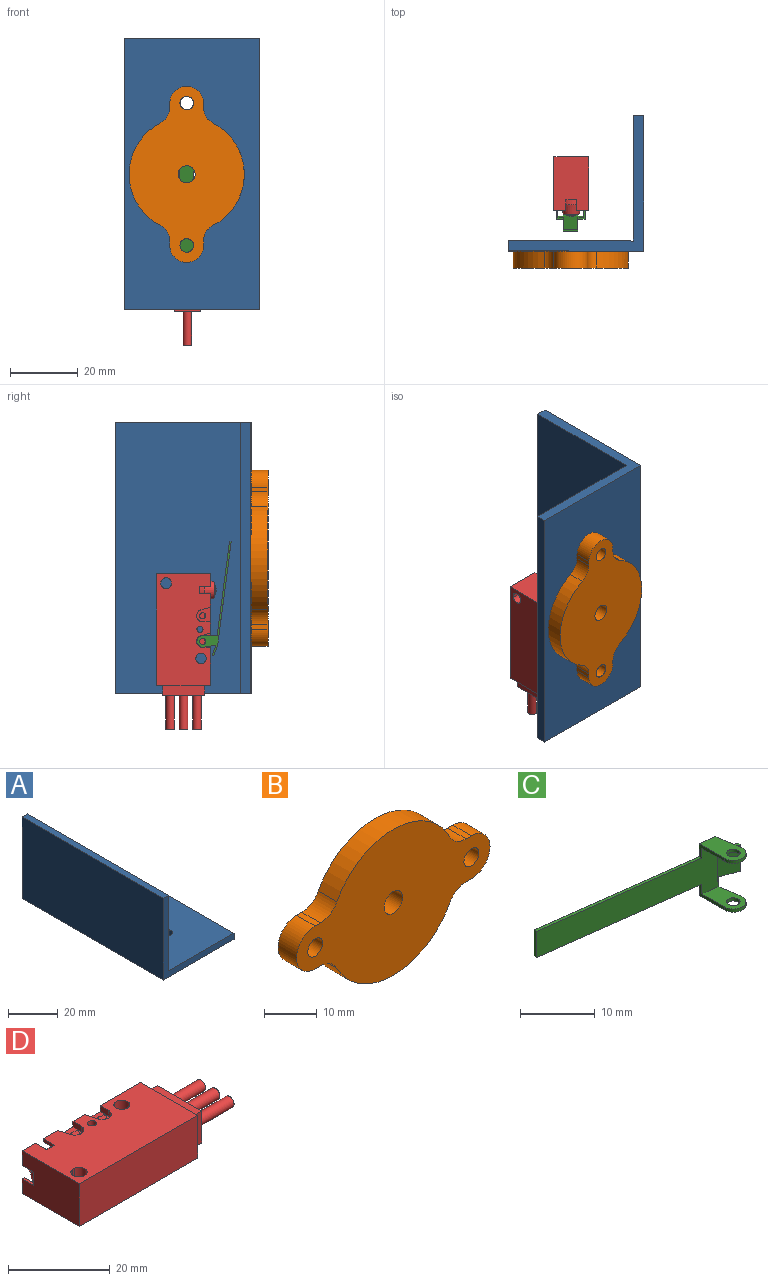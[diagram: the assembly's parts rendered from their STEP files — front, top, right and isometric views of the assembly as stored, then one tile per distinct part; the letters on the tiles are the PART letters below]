
ASSEMBLY  parts=4 mates=8
PART A: 11 faces, bbox 40x80x40 mm
  f0: plane 80x40mm, normal (-1,0,0), area 3200mm2, adj f1,f5,f6,f7
  f1: plane 80x40mm, normal (0,0,-1), area 3124.6mm2, adj f0,f2,f6,f7,f8,f9,f10
  f2: plane 80x3mm, normal (1,0,0), area 240mm2, adj f1,f3,f6,f7
  f3: plane 80x37mm, normal (0,0,1), area 2884.6mm2, adj f2,f4,f6,f7,f8,f9,f10
  f4: plane 80x37mm, normal (1,0,0), area 2960mm2, adj f3,f5,f6,f7
  f5: plane 80x3mm, normal (0,0,1), area 240mm2, adj f0,f4,f6,f7
  f6: plane 40x40mm, normal (0,-1,0), area 231mm2, adj f0,f1,f2,f3,f4,f5
  f7: plane 40x40mm, normal (0,1,0), area 231mm2, adj f0,f1,f2,f3,f4,f5
  f8: cylinder r=2mm len=4mm, axis (0,0,1), area 37.7mm2, adj f1,f3
  f9: cylinder r=2mm len=4mm, axis (0,0,1), area 37.7mm2, adj f1,f3
  f10: cylinder r=4mm len=8mm, axis (0,0,1), area 75.4mm2, adj f1,f3
PART B: 17 faces, bbox 52x5x34 mm
  f0: plane 5x1.4mm, normal (0,0,1), area 7mm2, adj f1,f14,f15,f16
  f1: cylinder r=5mm len=10mm, axis (0,1,0), area 78.5mm2, adj f0,f2,f15,f16
  f2: plane 5x1.4mm, normal (0,0,-1), area 7mm2, adj f1,f3,f15,f16
  f3: cylinder r=5mm len=5mm, axis (0,1,0), area 27.5mm2, adj f2,f4,f15,f16
  f4: cylinder r=17mm len=30.28mm, axis (0,1,0), area 186.8mm2, adj f3,f5,f15,f16
  f5: cylinder r=5mm len=5mm, axis (0,1,0), area 27.5mm2, adj f4,f6,f15,f16
  f6: plane 5x1.4mm, normal (0,0,-1), area 7mm2, adj f5,f7,f15,f16
  f7: cylinder r=5mm len=10mm, axis (0,1,0), area 78.5mm2, adj f6,f8,f15,f16
  f8: plane 5x1.4mm, normal (0,0,1), area 7mm2, adj f7,f9,f15,f16
  f9: cylinder r=5mm len=5mm, axis (0,1,0), area 27.5mm2, adj f8,f10,f15,f16
  f10: cylinder r=17mm len=30.28mm, axis (0,1,0), area 186.8mm2, adj f9,f14,f15,f16
  f11: cylinder r=2mm len=5mm, axis (0,1,0), area 62.8mm2, adj f15,f16
  f12: cylinder r=2mm len=5mm, axis (0,1,0), area 62.8mm2, adj f15,f16
  f13: cylinder r=2.5mm len=5mm, axis (0,1,0), area 78.5mm2, adj f15,f16
  f14: cylinder r=5mm len=5mm, axis (0,1,0), area 27.5mm2, adj f0,f10,f15,f16
  f15: plane 52x34mm, normal (0,-1,0), area 1034mm2, adj f0,f1,f2,f3,f4,f5,f6,f7
  f16: plane 52x34mm, normal (0,1,0), area 1034mm2, adj f0,f1,f2,f3,f4,f5,f6,f7
PART C: 24 faces, bbox 33.7x10.1x8.5 mm
  f0: plane 7.5x3.11mm, normal (-0.34,-0.94,0), area 14.6mm2, adj f1,f3,f12,f13,f14,f15,f18,f20
  f1: plane 30.45x7.5mm, normal (-0.13,-0.99,0), area 140.7mm2, adj f0,f6,f8,f9,f10,f11,f18,f20
  f2: plane 4.3x3.16mm, normal (0.34,0.94,0), area 14.5mm2, adj f3,f7,f13,f15
  f3: plane 4.3x0.47mm, normal (0.94,-0.34,0), area 2.1mm2, adj f0,f2,f13,f15
  f4: plane 6.47x3.4mm, normal (0,0,1), area 16mm2, adj f7,f10,f14,f16,f17,f19
  f5: plane 6.47x3.4mm, normal (0,0,-1), area 16mm2, adj f7,f8,f12,f21,f22,f23
  f6: plane 4.3x0.5mm, normal (-0.99,0.13,0), area 2.2mm2, adj f1,f7,f9,f11
  f7: plane 30.5x8.5mm, normal (0.13,0.99,0), area 144.1mm2, adj f2,f4,f5,f6,f8,f9,f10,f11
  f8: plane 4.77x2.1mm, normal (-1,0,0), area 3.2mm2, adj f1,f5,f7,f9,f20,f21
  f9: plane 27.77x4.14mm, normal (0,0,-1), area 14mm2, adj f1,f6,f7,f8
  f10: plane 4.77x2.1mm, normal (-1,0,0), area 3.2mm2, adj f1,f4,f7,f11,f16,f18
  f11: plane 27.77x4.14mm, normal (0,0,1), area 14mm2, adj f1,f6,f7,f10
  f12: plane 2.1x0.53mm, normal (1,0,0), area 1.1mm2, adj f0,f5,f7,f13,f22
  f13: plane 3.16x1.63mm, normal (0,0,-1), area 1.6mm2, adj f0,f2,f3,f12
  f14: plane 2.1x0.53mm, normal (1,0,0), area 1.1mm2, adj f0,f4,f7,f15,f17
  f15: plane 3.16x1.63mm, normal (0,0,1), area 1.6mm2, adj f0,f2,f3,f14
  f16: cylinder r=1.7mm len=3.4mm, axis (0,0,1), area 2.8mm2, adj f4,f10,f17,f18
  f17: plane 3.6x0.58mm, normal (0.99,0.16,0), area 1.8mm2, adj f4,f14,f16,f18
  f18: plane 5.96x3.4mm, normal (0,0,-1), area 14.6mm2, adj f0,f1,f10,f16,f17,f19
  f19: cylinder r=0.9mm len=1.8mm, axis (0,0,1), area 2.8mm2, adj f4,f18
  f20: plane 5.96x3.4mm, normal (0,0,1), area 14.6mm2, adj f0,f1,f8,f21,f22,f23
  f21: cylinder r=1.7mm len=3.4mm, axis (0,0,-1), area 2.8mm2, adj f5,f8,f20,f22
  f22: plane 3.6x0.58mm, normal (0.99,0.16,0), area 1.8mm2, adj f5,f12,f20,f21
  f23: cylinder r=0.9mm len=1.8mm, axis (0,0,-1), area 2.8mm2, adj f5,f20
PART D: 84 faces, bbox 45.9x17.6x10.3 mm
  f0: plane 27.1x10.3mm, normal (0,1,0), area 160.5mm2, adj f6,f7,f9,f12,f14,f21,f22,f23
  f1: cylinder r=0.9mm len=1.8mm, axis (0,0,1), area 3mm2, adj f2,f6,f72,f73
  f2: plane 1.8x1.3mm, normal (0,0,-1), area 2mm2, adj f1,f72
  f3: cylinder r=0.9mm len=1.8mm, axis (0,0,1), area 3mm2, adj f4,f7,f70,f71
  f4: plane 1.8x1.3mm, normal (0,0,-1), area 2mm2, adj f3,f70
  f5: plane 12.4x7.7mm, normal (1,0,0), area 80.8mm2, adj f42,f43,f44,f45,f60,f62,f64
  f6: plane 4.36x4.1mm, normal (0,0,-1), area 11.8mm2, adj f0,f1,f28,f29,f30
  f7: plane 4.36x4.1mm, normal (0,0,-1), area 11.8mm2, adj f0,f3,f31,f32,f33
  f8: plane 3.7x3.55mm, normal (0,1,0), area 7.4mm2, adj f11,f14,f46,f47,f48
  f9: plane 15.9x10.3mm, normal (1,0,0), area 68.3mm2, adj f0,f12,f13,f14,f42,f43,f44,f45
  f10: plane 3.7x3.55mm, normal (0,1,0), area 7.4mm2, adj f11,f12,f52,f53,f54
  f11: plane 15.9x10.3mm, normal (-1,0,0), area 153.5mm2, adj f8,f10,f12,f13,f14,f46,f54,f55
  f12: plane 33x15.9mm, normal (0,0,1), area 470.9mm2, adj f0,f9,f10,f11,f13,f15,f16,f17
  f13: plane 33x10.3mm, normal (0,-1,0), area 339.9mm2, adj f9,f11,f12,f14
  f14: plane 33x15.9mm, normal (0,0,-1), area 470.9mm2, adj f0,f8,f9,f11,f13,f15,f16,f17
  f15: cylinder r=1.55mm len=10.3mm, axis (0,0,1), area 100.3mm2, adj f12,f14
  f16: cylinder r=1.6mm len=10.3mm, axis (0,0,1), area 43.5mm2, adj f12,f14,f17,f19
  f17: plane 10.3x0.79mm, normal (0,-1,0), area 8.2mm2, adj f12,f14,f16,f18
  f18: cylinder r=1.6mm len=10.3mm, axis (0,0,1), area 43.5mm2, adj f12,f14,f17,f19
  f19: plane 10.3x0.79mm, normal (0,1,0), area 8.2mm2, adj f12,f14,f16,f18
  f20: cylinder r=1.8mm len=3.53mm, axis (0,0,1), area 7.2mm2, adj f12,f21,f22,f23
  f21: plane 2.81x1.4mm, normal (0.96,0.28,0), area 4.1mm2, adj f0,f12,f20,f23
  f22: plane 2.3x1.4mm, normal (-1,0,0), area 3.2mm2, adj f0,f12,f20,f23
  f23: plane 4.36x4.1mm, normal (0,0,1), area 11.8mm2, adj f0,f20,f21,f22,f58
  f24: cylinder r=1.8mm len=3.53mm, axis (0,0,1), area 7.2mm2, adj f12,f25,f26,f27
  f25: plane 2.81x1.4mm, normal (0.96,0.28,0), area 4.1mm2, adj f0,f12,f24,f27
  f26: plane 2.3x1.4mm, normal (-1,0,0), area 3.2mm2, adj f0,f12,f24,f27
  f27: plane 4.36x4.1mm, normal (0,0,1), area 11.8mm2, adj f0,f24,f25,f26,f56
  f28: cylinder r=1.8mm len=3.53mm, axis (0,0,-1), area 7.2mm2, adj f6,f14,f29,f30
  f29: plane 2.3x1.4mm, normal (-1,0,0), area 3.2mm2, adj f0,f6,f14,f28
  f30: plane 2.81x1.4mm, normal (0.96,0.28,0), area 4.1mm2, adj f0,f6,f14,f28
  f31: cylinder r=1.8mm len=3.53mm, axis (0,0,-1), area 7.2mm2, adj f7,f14,f32,f33
  f32: plane 2.3x1.4mm, normal (-1,0,0), area 3.2mm2, adj f0,f7,f14,f31
  f33: plane 2.81x1.4mm, normal (0.96,0.28,0), area 4.1mm2, adj f0,f7,f14,f31
  f34: plane 4.8x4.1mm, normal (1,0,0), area 19.7mm2, adj f0,f37,f38,f39
  f35: plane 4.8x1.3mm, normal (-0.71,0.71,0), area 8.8mm2, adj f0,f36,f38,f39
  f36: plane 4.8x2.8mm, normal (-1,0,0), area 13.4mm2, adj f35,f37,f38,f39
  f37: plane 11.5x4.8mm, normal (0,1,0), area 55.2mm2, adj f34,f36,f38,f39
  f38: plane 12.8x4.1mm, normal (0,0,1), area 45.5mm2, adj f0,f34,f35,f36,f37,f41
  f39: plane 12.8x4.1mm, normal (0,0,-1), area 45.5mm2, adj f0,f34,f35,f36,f37,f40
  f40: cylinder r=0.9mm len=2.75mm, axis (0,0,1), area 15.6mm2, adj f12,f39
  f41: cylinder r=0.9mm len=2.75mm, axis (0,0,1), area 15.6mm2, adj f14,f38
  f42: plane 12.4x2.9mm, normal (0,0,1), area 36mm2, adj f5,f9,f43,f45
  f43: plane 7.7x2.9mm, normal (0,-1,0), area 22.3mm2, adj f5,f9,f42,f44
  f44: plane 12.4x2.9mm, normal (0,0,-1), area 36mm2, adj f5,f9,f43,f45
  f45: plane 7.7x2.9mm, normal (0,1,0), area 22.3mm2, adj f5,f9,f42,f44
  f46: plane 3.2x0.59mm, normal (0,0,1), area 1.9mm2, adj f8,f11,f47,f55
  f47: cylinder r=4.5mm len=3.2mm, axis (0,1,0), area 13.8mm2, adj f8,f46,f48,f55
  f48: plane 3.2x0.79mm, normal (1,0,0), area 2.5mm2, adj f8,f14,f47,f55
  f49: plane 3.2x0.79mm, normal (-1,0,0), area 2.5mm2, adj f0,f14,f50,f55
  f50: cylinder r=4.5mm len=8.73mm, axis (0,1,0), area 38.1mm2, adj f0,f49,f51,f55
  f51: plane 3.2x0.79mm, normal (-1,0,0), area 2.5mm2, adj f0,f12,f50,f55
  f52: plane 3.2x0.79mm, normal (1,0,0), area 2.5mm2, adj f10,f12,f53,f55
  f53: cylinder r=4.5mm len=3.2mm, axis (0,1,0), area 13.8mm2, adj f10,f52,f54,f55
  f54: plane 3.2x0.59mm, normal (0,0,-1), area 1.9mm2, adj f10,f11,f53,f55
  f55: plane 10.3x9.3mm, normal (0,1,0), area 15.1mm2, adj f11,f12,f14,f46,f47,f48,f49,f50
  f56: cylinder r=0.9mm len=1.8mm, axis (0,0,-1), area 3mm2, adj f27,f57,f66,f67
  f57: plane 1.8x1.3mm, normal (0,0,1), area 2mm2, adj f56,f66
  f58: cylinder r=0.9mm len=1.8mm, axis (0,0,-1), area 3mm2, adj f23,f59,f68,f69
  f59: plane 1.8x1.3mm, normal (0,0,1), area 2mm2, adj f58,f68
  f60: cylinder r=1.25mm len=10mm, axis (-1,0,0), area 78.5mm2, adj f5,f61
  f61: plane 2.5x2.5mm, normal (1,0,0), area 4.9mm2, adj f60
  f62: cylinder r=1.25mm len=10mm, axis (-1,0,0), area 78.5mm2, adj f5,f63
  f63: plane 2.5x2.5mm, normal (1,0,0), area 4.9mm2, adj f62
  f64: cylinder r=1.25mm len=10mm, axis (-1,0,0), area 78.5mm2, adj f5,f65
  f65: plane 2.5x2.5mm, normal (1,0,0), area 4.9mm2, adj f64
  f66: plane 1.61x0.35mm, normal (0,1,0), area 0.6mm2, adj f56,f57,f67
  f67: plane 1.61x0.5mm, normal (0,0,1), area 0.6mm2, adj f56,f66
  f68: plane 1.61x0.35mm, normal (0,1,0), area 0.6mm2, adj f58,f59,f69
  f69: plane 1.61x0.5mm, normal (0,0,1), area 0.6mm2, adj f58,f68
  f70: plane 1.61x0.35mm, normal (0,1,0), area 0.6mm2, adj f3,f4,f71
  f71: plane 1.61x0.5mm, normal (0,0,-1), area 0.6mm2, adj f3,f70
  f72: plane 1.61x0.35mm, normal (0,1,0), area 0.6mm2, adj f1,f2,f73
  f73: plane 1.61x0.5mm, normal (0,0,-1), area 0.6mm2, adj f1,f72
  f74: plane 4.3x1.44mm, normal (-1,0,0), area 6.2mm2, adj f0,f75,f76,f77
  f75: plane 4.3x2.5mm, normal (0.5,0.87,0), area 12.4mm2, adj f0,f74,f76,f77
  f76: plane 2.5x1.44mm, normal (0,0,1), area 1.8mm2, adj f0,f74,f75
  f77: plane 2.5x1.44mm, normal (0,0,-1), area 1.8mm2, adj f0,f74,f75
  f78: cylinder r=1.25mm len=2.5mm, axis (0,1,0), area 2mm2, adj f79,f83
  f79: plane 4.54x4.54mm, normal (0,1,0), area 11.3mm2, adj f78,f80
  f80: cone r=2.27mm half-angle=16.9deg, axis (0,-1,0), area 53.7mm2, adj f79,f81
  f81: plane 8.2x8.2mm, normal (0,1,0), area 21mm2, adj f80,f82
  f82: cylinder r=4.1mm len=8.2mm, axis (0,1,0), area 36.1mm2, adj f55,f81
  f83: sphere r=4.2mm, area 5mm2, adj f78
PLACE A rot(axis=(0,0.71,0.71),179.9deg) t=(-34.21,-104.43,-25.45)mm
PLACE B rot(axis=(0,-1,0),90deg) t=(-55.71,-104.38,-86.45)mm
PLACE C rot(axis=(-0.71,0,0.71),179.9deg) t=(-55.73,-90.09,-90.02)mm
PLACE D rot(axis=(-0.71,0,0.71),179.9deg) t=(-55.55,-89.59,-95.02)mm
MATE revolute D.f3 <-> C.f16  axis (-1,0,0) through (-51.48,-90.1,-90.02)mm
MATE parallel D.f14 <-> A.f4  axis (1,0,0) through (-50.39,-83.96,-86.82)mm
MATE cylindrical A.f8 <-> B.f11  axis (0,1,0) through (-55.7,-101.38,-86.45)mm
MATE parallel D.f11 <-> A.f7  axis (0,0,1) through (-57.15,-89.19,-70.02)mm
MATE planar A.f1 <-> B.f16  axis (0,-1,0) through (-54.17,-104.38,-65.45)mm
MATE parallel C.f18 <-> D.f27  axis (1,0,0) through (-59.48,-92.15,-91.41)mm
MATE cylindrical B.f7 <-> A.f9  axis (0,-1,0) through (-55.72,-109.38,-44.45)mm
MATE cylindrical B.f11 <-> A.f8  axis (0,1,0) through (-55.71,-104.38,-86.45)mm
